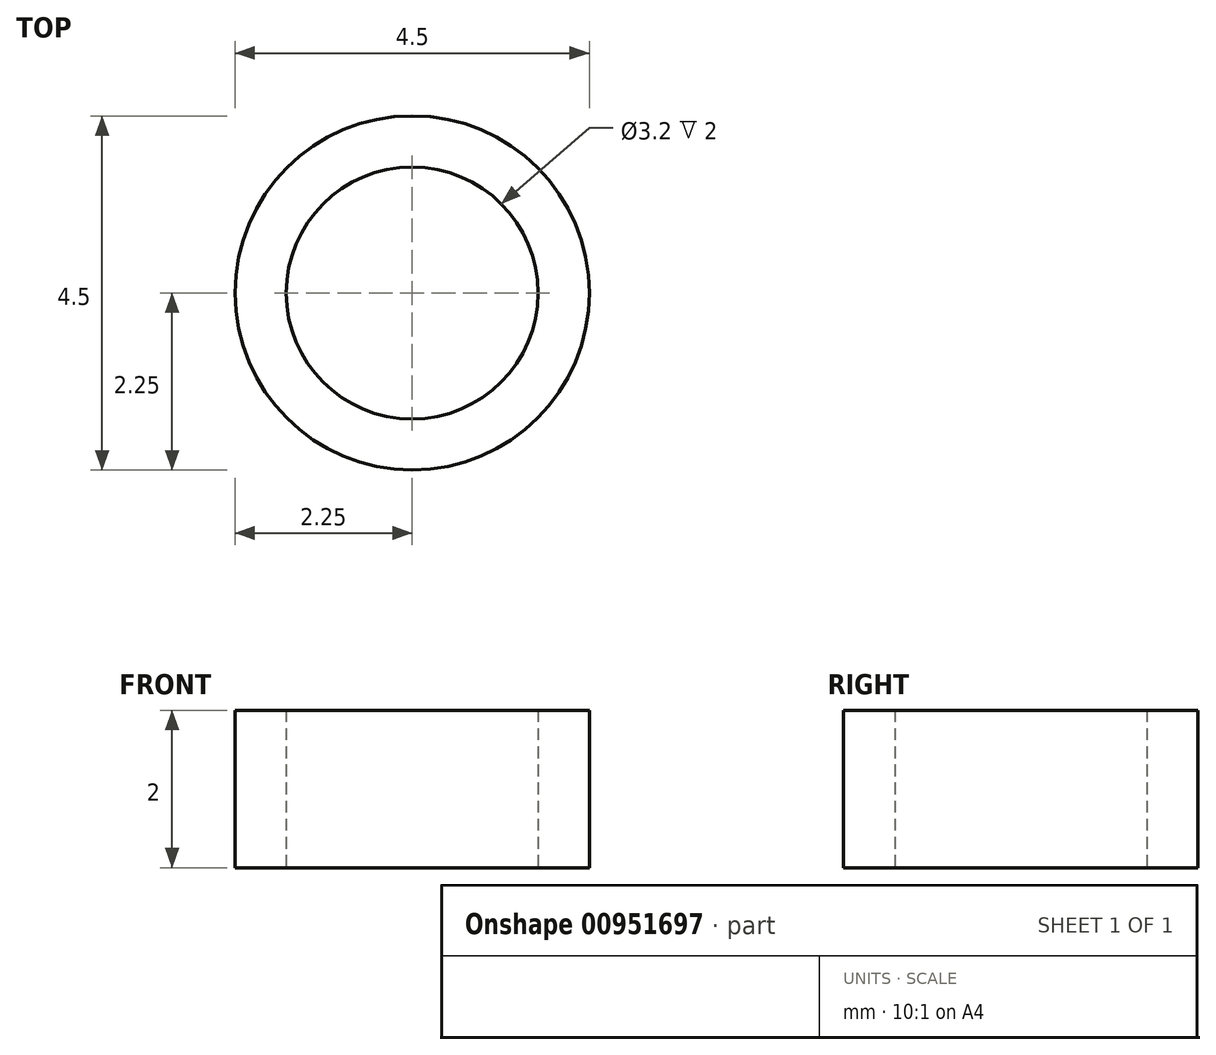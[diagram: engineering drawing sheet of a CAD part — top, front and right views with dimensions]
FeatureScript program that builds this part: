
annotation { "Feature Type Name" : "Feature", "Feature Type Description" : "" }
export const myFeature = defineFeature(function(context is Context, id is Id, definition is map)
    precondition{}
    {
        {
            var Q0;
            Q0=qCreatedBy(makeId("Top.planeOp"), FACE);
            var sketch = newSketch(context, id + "F0", { "sketchPlane" : qUnion([Q0])});
            skCircle(sketch, "E0", {"center": v(0, 0) * mm, "radius": 1.6 * mm});
            skCircle(sketch, "E1", {"center": v(0, 0) * mm, "radius": 2.25 * mm});
            skSolve(sketch);
        }
        {
            var Q0;
            Q0 = qSketchRegion(id + "F0", true);
            extrude(context, id + "F1", {"entities" : qUnion([Q0]), "domain" : OperationDomain.MODEL, "flatOperationType" : FlatOperationType.REMOVE, "depth" : 2 * mm, "offsetDistance" : 25 * mm});
        }
    });
